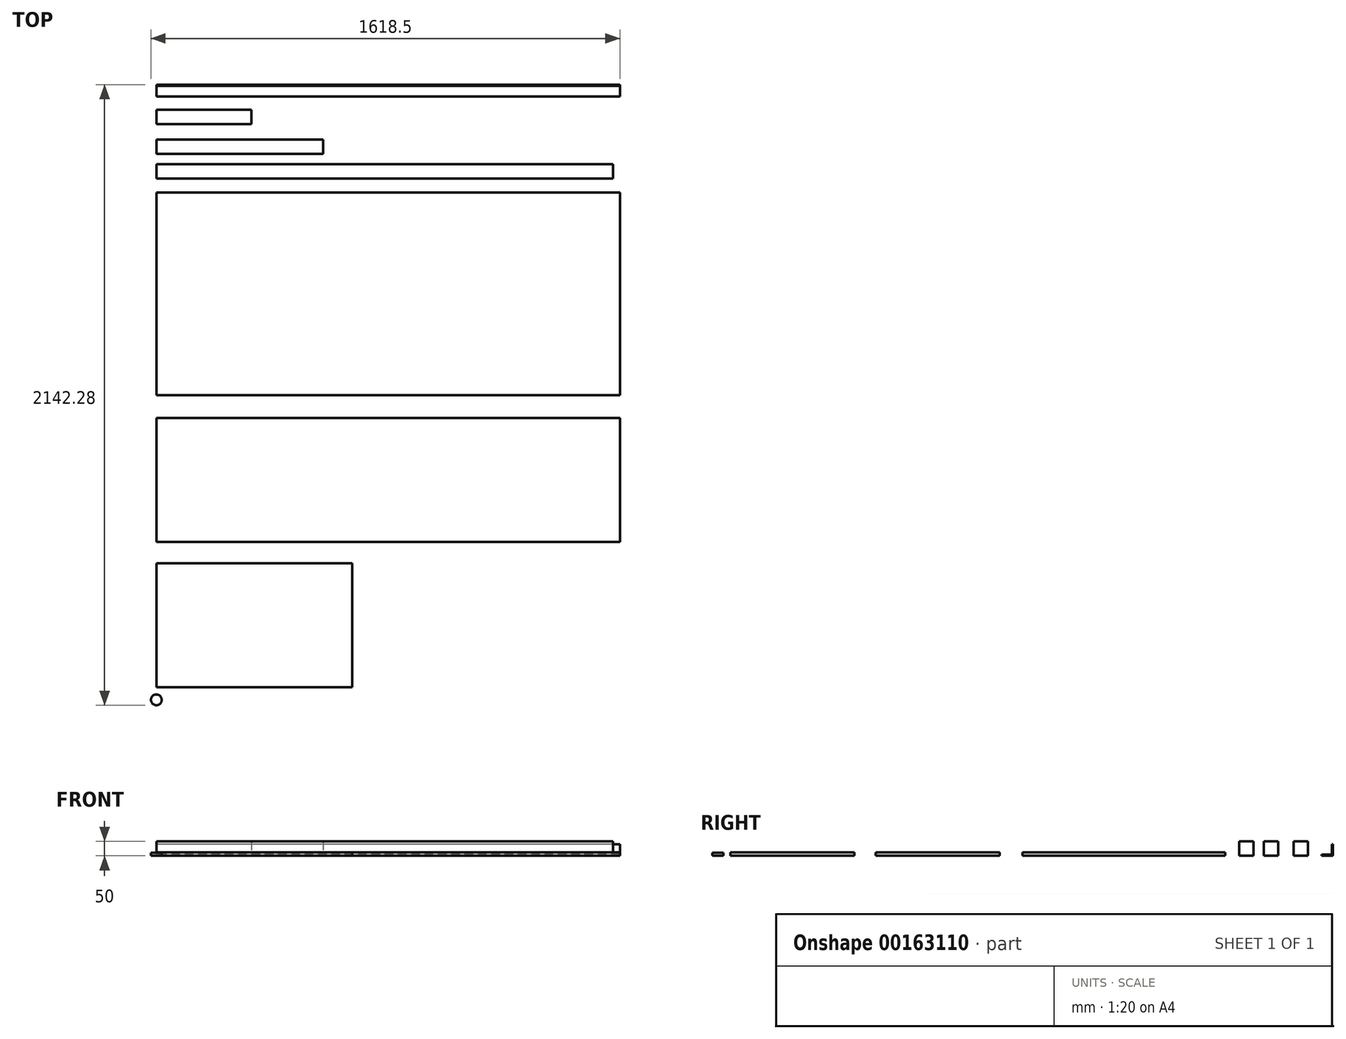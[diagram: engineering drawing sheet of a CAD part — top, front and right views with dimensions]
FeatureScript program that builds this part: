
annotation { "Feature Type Name" : "Feature", "Feature Type Description" : "" }
export const myFeature = defineFeature(function(context is Context, id is Id, definition is map)
    precondition{}
    {
        {
            assignVariable(context, id + "F0", {"name" : "length", "anyValue" : 1600});
        }
        {
            assignVariable(context, id + "F1", {"name" : "thick", "anyValue" : 12});
        }
        {
            assignVariable(context, id + "F2", {"name" : "tasseau", "anyValue" : 50});
        }
        {
            assignVariable(context, id + "F3", {"name" : "feet", "anyValue" : 10});
        }
        {
            var Q0;
            Q0=qCreatedBy(makeId("Top.planeOp"),FACE);
            var sketch = newSketch(context, id + "F4", { "sketchPlane" : qUnion([Q0])});
            skLineSegment(sketch, "E0.bottom", {"start": v(0, 0) * mm, "end": v(1576, 0) * mm});
            skLineSegment(sketch, "E0.top", {"start": v(0, 50) * mm, "end": v(1576, 50) * mm});
            skLineSegment(sketch, "E0.left", {"start": v(0, 0) * mm, "end": v(0, 50) * mm});
            skLineSegment(sketch, "E0.right", {"start": v(1576, 0) * mm, "end": v(1576, 50) * mm});
            skSolve(sketch);
        }
        {
            var Q0;
            Q0 = qSketchRegion(id + "F4", true);
            extrude(context, id + "F5", {"entities" : qUnion([Q0]), "depth" : (getVariable(context, 'tasseau')) * mm});
        }
        {
            var Q0;
            Q0=qCreatedBy(makeId("Top.planeOp"),FACE);
            var sketch = newSketch(context, id + "F6", { "sketchPlane" : qUnion([Q0])});
            skLineSegment(sketch, "E1.bottom", {"start": v(0, 85.12) * mm, "end": v(576, 85.12) * mm});
            skLineSegment(sketch, "E1.top", {"start": v(0, 135.12) * mm, "end": v(576, 135.12) * mm});
            skLineSegment(sketch, "E1.left", {"start": v(0, 85.12) * mm, "end": v(0, 135.12) * mm});
            skLineSegment(sketch, "E1.right", {"start": v(576, 85.12) * mm, "end": v(576, 135.12) * mm});
            skSolve(sketch);
        }
        {
            var Q0;
            Q0 = qSketchRegion(id + "F6", true);
            extrude(context, id + "F7", {"entities" : qUnion([Q0]), "depth" : (getVariable(context, 'tasseau')) * mm});
        }
        {
            var Q0;
            Q0=qCreatedBy(makeId("Top.planeOp"),FACE);
            var sketch = newSketch(context, id + "F8", { "sketchPlane" : qUnion([Q0])});
            skLineSegment(sketch, "E2.bottom", {"start": v(0, 187.93) * mm, "end": v(328, 187.93) * mm});
            skLineSegment(sketch, "E2.top", {"start": v(0, 237.93) * mm, "end": v(328, 237.93) * mm});
            skLineSegment(sketch, "E2.left", {"start": v(0, 187.93) * mm, "end": v(0, 237.93) * mm});
            skLineSegment(sketch, "E2.right", {"start": v(328, 187.93) * mm, "end": v(328, 237.93) * mm});
            skSolve(sketch);
        }
        {
            var Q0;
            Q0 = qSketchRegion(id + "F8", true);
            extrude(context, id + "F9", {"entities" : qUnion([Q0]), "depth" : (getVariable(context, 'tasseau')) * mm});
        }
        {
            var Q0;
            Q0=qCreatedBy(makeId("Top.planeOp"),FACE);
            var sketch = newSketch(context, id + "F10", { "sketchPlane" : qUnion([Q0])});
            skLineSegment(sketch, "E3.bottom", {"start": v(0, -47.86) * mm, "end": v(1600, -47.86) * mm});
            skLineSegment(sketch, "E3.top", {"start": v(0, -747.86) * mm, "end": v(1600, -747.86) * mm});
            skLineSegment(sketch, "E3.left", {"start": v(0, -47.86) * mm, "end": v(0, -747.86) * mm});
            skLineSegment(sketch, "E3.right", {"start": v(1600, -47.86) * mm, "end": v(1600, -747.86) * mm});
            skSolve(sketch);
        }
        {
            var Q0;
            Q0 = qSketchRegion(id + "F10", true);
            extrude(context, id + "F11", {"entities" : qUnion([Q0]), "depth" : (getVariable(context, 'thick')) * mm});
        }
        {
            var Q0;
            Q0=qCreatedBy(makeId("Top.planeOp"),FACE);
            var sketch = newSketch(context, id + "F12", { "sketchPlane" : qUnion([Q0])});
            skLineSegment(sketch, "E4.bottom", {"start": v(0, -826.42) * mm, "end": v(1600, -826.42) * mm});
            skLineSegment(sketch, "E4.top", {"start": v(0, -1254.42) * mm, "end": v(1600, -1254.42) * mm});
            skLineSegment(sketch, "E4.left", {"start": v(0, -826.42) * mm, "end": v(0, -1254.42) * mm});
            skLineSegment(sketch, "E4.right", {"start": v(1600, -826.42) * mm, "end": v(1600, -1254.42) * mm});
            skSolve(sketch);
        }
        {
            var Q0;
            Q0 = qSketchRegion(id + "F12", true);
            extrude(context, id + "F13", {"entities" : qUnion([Q0]), "depth" : (getVariable(context, 'thick')) * mm});
        }
        {
            var Q0;
            Q0=qCreatedBy(makeId("Top.planeOp"),FACE);
            var sketch = newSketch(context, id + "F14", { "sketchPlane" : qUnion([Q0])});
            skLineSegment(sketch, "E5.bottom", {"start": v(0, -1328.28) * mm, "end": v(676, -1328.28) * mm});
            skLineSegment(sketch, "E5.top", {"start": v(0, -1756.28) * mm, "end": v(676, -1756.28) * mm});
            skLineSegment(sketch, "E5.left", {"start": v(0, -1328.28) * mm, "end": v(0, -1756.28) * mm});
            skLineSegment(sketch, "E5.right", {"start": v(676, -1328.28) * mm, "end": v(676, -1756.28) * mm});
            skSolve(sketch);
        }
        {
            var Q0;
            Q0 = qSketchRegion(id + "F14", true);
            extrude(context, id + "F15", {"entities" : qUnion([Q0]), "depth" : (getVariable(context, 'thick')) * mm});
        }
        {
            var Q0;
            Q0=qCreatedBy(makeId("Right.planeOp"),FACE);
            var sketch = newSketch(context, id + "F16", { "sketchPlane" : qUnion([Q0])});
            skLineSegment(sketch, "E6", {"start": v(324.13, 0) * mm, "end": v(324.13, 40) * mm});
            skLineSegment(sketch, "E7", {"start": v(324.13, 40) * mm, "end": v(320.13, 40) * mm});
            skLineSegment(sketch, "E8", {"start": v(320.13, 40) * mm, "end": v(320.13, 4) * mm});
            skLineSegment(sketch, "E9", {"start": v(320.13, 4) * mm, "end": v(284.13, 4) * mm});
            skLineSegment(sketch, "E10", {"start": v(284.13, 4) * mm, "end": v(284.13, 0) * mm});
            skLineSegment(sketch, "E11", {"start": v(284.13, 0) * mm, "end": v(324.13, 0) * mm});
            skSolve(sketch);
        }
        {
            var Q0;
            Q0 = qSketchRegion(id + "F16", true);
            extrude(context, id + "F17", {"entities" : qUnion([Q0]), "depth" : (getVariable(context, 'length')) * mm});
        }
        {
            var Q0;
            Q0=qCreatedBy(makeId("Top.planeOp"),FACE);
            var sketch = newSketch(context, id + "F18", { "sketchPlane" : qUnion([Q0])});
            skCircle(sketch, "E12", {"center": v(0, -1799.65) * mm, "radius": 18.5 * mm});
            skSolve(sketch);
        }
        {
            var Q0;
            Q0 = qSketchRegion(id + "F18", true);
            extrude(context, id + "F19", {"entities" : qUnion([Q0]), "depth" : (getVariable(context, 'feet')) * mm});
        }
    });
